# Revit family: BIM_RGV_INFINITY_F4_DN40_DN300_PN10_16_HDW
name_source: partatom
category: Generic Models
revit_build: Autodesk Revit 2017 (Build: 20160225_1515(x64)
units: mm (PartAtom-declared; Revit-internal decimal feet)

## family parameters
Always vertical = Yes
Can host rebar = No
Cut with Voids When Loaded = No
Part Type = Normal
Room Calculation Point = No
Round Connector Dimension = Use Diameter
Shared = No
Work Plane-Based = No

## types (10) — shared parameters

## per-type parameters (varying)
| type | HDW_DN100 | HDW_DN125 | HDW_DN150 | HDW_DN200 | HDW_DN250 | HDW_DN300 | HDW_DN40 | HDW_DN50 | HDW_DN65 | HDW_DN80 | Nominal_dia |
| DN300 | No | No | No | No | No | Yes | No | No | No | No | 300 mm  [stored 0.984252 ft] |
| DN250 | No | No | No | No | Yes | No | No | No | No | No | 250 mm  [stored 0.82021 ft] |
| DN200 | No | No | No | Yes | No | No | No | No | No | No | 200 mm  [stored 0.656168 ft] |
| DN150 | No | No | Yes | No | No | No | No | No | No | No | 150 mm  [stored 0.492126 ft] |
| DN100 | Yes | No | No | No | No | No | No | No | No | No | 100 mm  [stored 0.328084 ft] |
| DN80 | No | No | No | No | No | No | No | No | No | Yes | 80 mm  [stored 0.262467 ft] |
| DN65 | No | No | No | No | No | No | No | No | Yes | No | 65 mm  [stored 0.213255 ft] |
| DN50 | No | No | No | No | No | No | No | Yes | No | No | 50 mm  [stored 0.164042 ft] |
| DN125 | No | Yes | No | No | No | No | No | No | No | No | 125 mm  [stored 0.410105 ft] |
| DN40 | No | No | No | No | No | No | Yes | No | No | No | 40 mm  [stored 0.131234 ft] |

note: [stored X ft] marks values corroborated as IEEE doubles in the binary element streams (Revit-internal decimal feet)

## geometry (parser evidence)
native form markers: Sweep x22
no freeform markers — native parametric forms only
